# Revit family: TOTUS2MIDI
name_source: partatom
category: Mechanical Equipment
revit_build: Autodesk Revit MEP 2013 (Build: 20120221_2030(x64)
units: mm (PartAtom-declared; Revit-internal decimal feet)

## types (1)
- TOTUS2MIDI
    AC Frequency Input = 50Hz nominal
    AC Voltage Input = 220-240 V AC (single phase)
    Category = Sentinel Totus 2
    Condensate = 10mm
    Country of Manufacture = UK
    Filters = 446603
    Height (excluding Spigots) = 350mm
    IP Rating - Commissioning Interface = IP42
    IP Rating - Unit = IPX4
    Length (excluding Spigots) = 1900mm
    Length (including Spigots) = 2020mm
    Manufacturer - Name = Vent-Axia Ltd
    Manufacturer - Website = www.vent-axia.com
    Motor Rating = 500W max
    Operating Humidity = 0% to 95% RH (non-condensing) – weatherproof unit option
    Operating Temperature = (-10C to +40C)
    Operational and Maintenance Manual = http://www.vent-axia.com
    Part Number = TOTUS2MIDI
    Product Description = Demand Energy Recovery Ventilation
    Spigot Diameter = 400mm x 250mm
    Warranty period = Unit 2 Years,Motor 5 Years
    Weight = 167kg
    Width (excluding suspension bracket) = 1250mm
    Width (including suspension bracket) = 1320mm

## geometry (parser evidence)
native form markers: Sweep x1
no freeform markers — native parametric forms only
